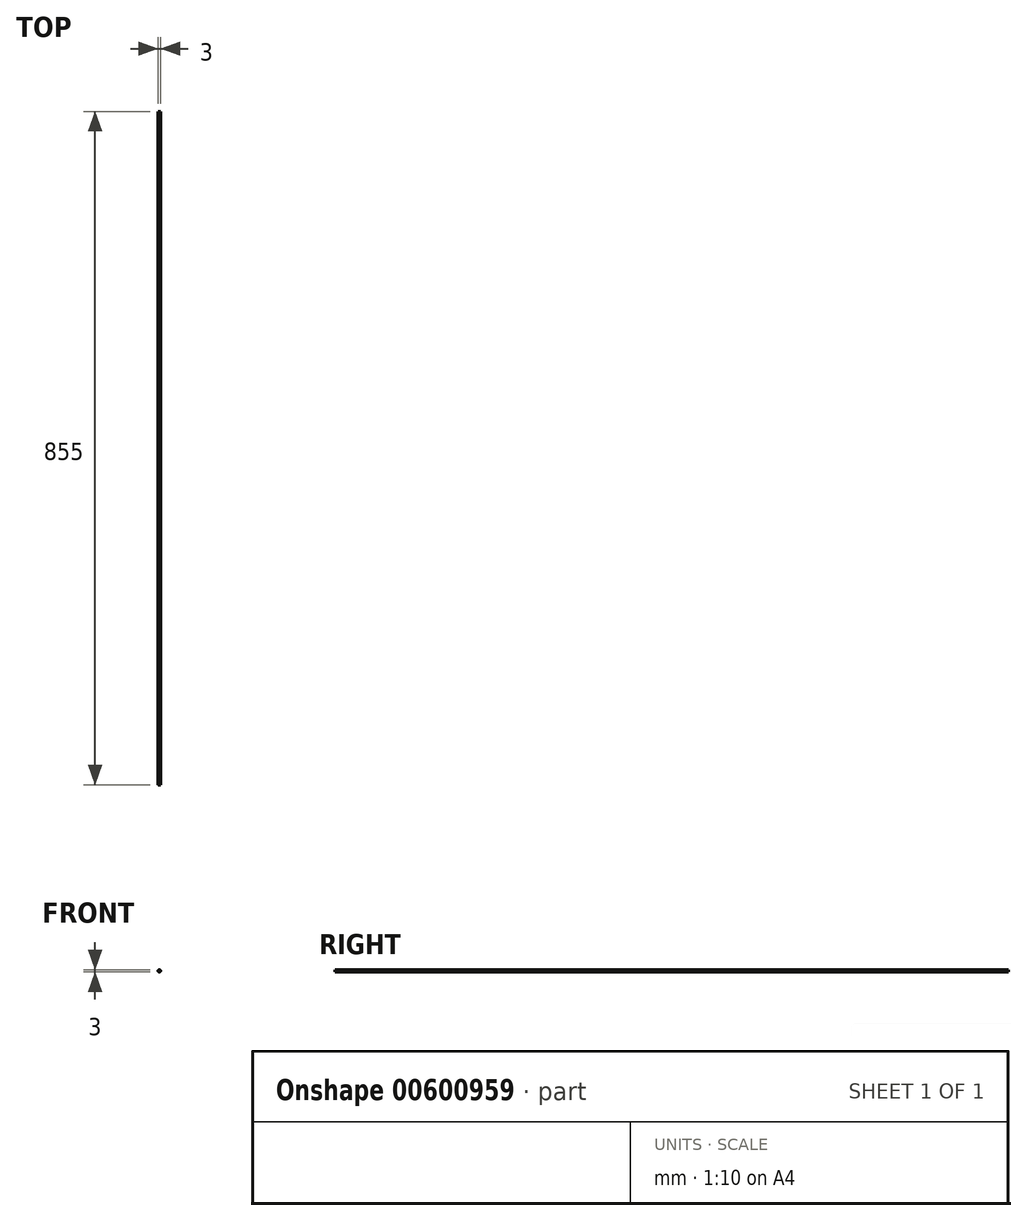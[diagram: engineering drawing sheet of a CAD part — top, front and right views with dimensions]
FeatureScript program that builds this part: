
annotation { "Feature Type Name" : "Feature", "Feature Type Description" : "" }
export const myFeature = defineFeature(function(context is Context, id is Id, definition is map)
    precondition{}
    {
        {
            var Q0;
            Q0=qCreatedBy(makeId("Front.planeOp"),FACE);
            var sketch = newSketch(context, id + "F0", { "sketchPlane" : qUnion([Q0])});
            skCircle(sketch, "E0", {"center": v(0, 0) * mm, "radius": 1.5 * mm});
            skSolve(sketch);
        }
        {
            var Q0;
            Q0=makeQuery(id+"F0.imprint","IMPRINT",FACE,{"disambiguationData":[TD([[makeQuery(id+"F0.imprint","IMPRINT",EDGE,{"derivedFrom":sQuery(id+"F0.wireOp",EDGE,"E0")}),1.0]])]});
            extrude(context, id + "F1", {"entities" : qUnion([Q0]), "depth" : 855 * mm, "offsetDistance" : 25 * mm});
        }
    });
